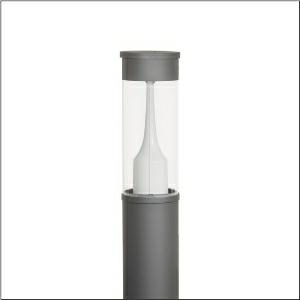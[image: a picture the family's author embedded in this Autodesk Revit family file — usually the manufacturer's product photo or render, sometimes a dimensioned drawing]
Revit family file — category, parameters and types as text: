
# Revit family: city-light_260_iq___p1_0a_5xa5295bf14h_d7c3
name_source: partatom
category: Lighting Fixtures
units: mm (PartAtom-declared; Revit-internal decimal feet)

## family parameters
Cut with Voids When Loaded = No
Host = Face
Light Source = No
Part Type = Normal
Room Calculation Point = No
Round Connector Dimension = Use Diameter
Shared = No

## types (1)
- --- (1 x LED, 1510 lm, 12.9 W, 2200K)
    Apparent Load = 13 VA
    CIE Flux Codes = 32 61 90 93 100
    Color Rendering = 70
    Color Temperature = 2200K
    Default Elevation = 1800 mm
    Description = City-Light 260 iQ, light pillar, Module 540 iQ-SR, primary light control with 3 zone facetted reflector, of plastic, silver coated, highly specular, structured, primary optical cover: cover, of PMMA, transparent, partly coated, light distribution: P1.0a, primary light characteristic: strongly asymmetric, LED, High Power LED, rated luminous flux: 1.510lm, luminous efficacy: 117lm/W, light colour: 722, colour temperature: 2200K, control gear: iQ Street-Remote, control: pre-setting: logarithmic dimming characteristic, Street-Remote, Auto-Match, Temp-Guard, Lumen-Switch, Night-Set, Smart-Wire, Light-Fading, Desk-Remote (wireless, voltage-free reading and setting of iQ features in the workshop via application-optimized NFC function/RFID function), optimised constant luminous flux control (CLO 2.0), with terminal, 6-pole, max. 2.5mm², mains connection: 230..240V, AC, 50/60Hz, start of lifetime: 13W, end of service life: 13W, reduction: 6W, luminaire housing, cylindrical, of extruded aluminium section, coated, Siteco® metallic grey (DB 702S), length: 2.600mm, diameter: 200mm, Module 540 iQ-SR, traffic white (RAL 9016), equipment: standard, protection rating (complete): IP65, insulation class (complete): insulation class II (safety insulation), certification: CE, ENEC, VDE, packaging unit: 1 piece

Light Distribution: P1.0a
    Height = 500 mm
    Lamp = 1 x LED
    Lamp Light Flux = 1510 lm
    Lamp Power = 12.9 W
    Lamp count = 1
    Length = 200 mm  [stored 0.656168 ft]
    Luminous efficacy = 117 lm/W
    Manufacturer = Siteco
    ModVariant = No
    Model = 5XA5295BF14H
    Mounting Place = Floor
    Mounting Type = Freestanding
    Number of Poles = 1
    OnlyDefault = Yes
    Power Factor = 1
    Product Name = City-Light 260 iQ | P1.0a
    Product group = light pillar
    ProductGroupID = 1301
    Protection Class = Protection class II
    Protection Degree = IP 65
    RLX_Detail_Level = 1
    RLX_Emergency_Light_Flux = 0 lm
    RLX_Emergency_Type = 0
    RLX_Emergency_Type_DB = No
    RlxData = <blob elided: 52949 chars, md5=df3436f3>
    Socket = socket
    Standby Power = 0 W
    System Light Flux = 1510 lm
    System Power = 13 W
    Type Comments = factory setting: luminous flux: 100 % | dim-lin: 254 | 516 mA
    Type Image = l_1006918.jpg
    URL = http://relux.com
    VarID = @adj_180995
    Voltage = 0 V
    Weight = 0.00 kg
    Width = 0 mm  [stored 0 ft]

note: [stored X ft] marks values corroborated as IEEE doubles in the binary element streams (Revit-internal decimal feet)

## geometry (parser evidence)
native form markers: Blend x4, Sweep x14
no freeform markers — native parametric forms only
